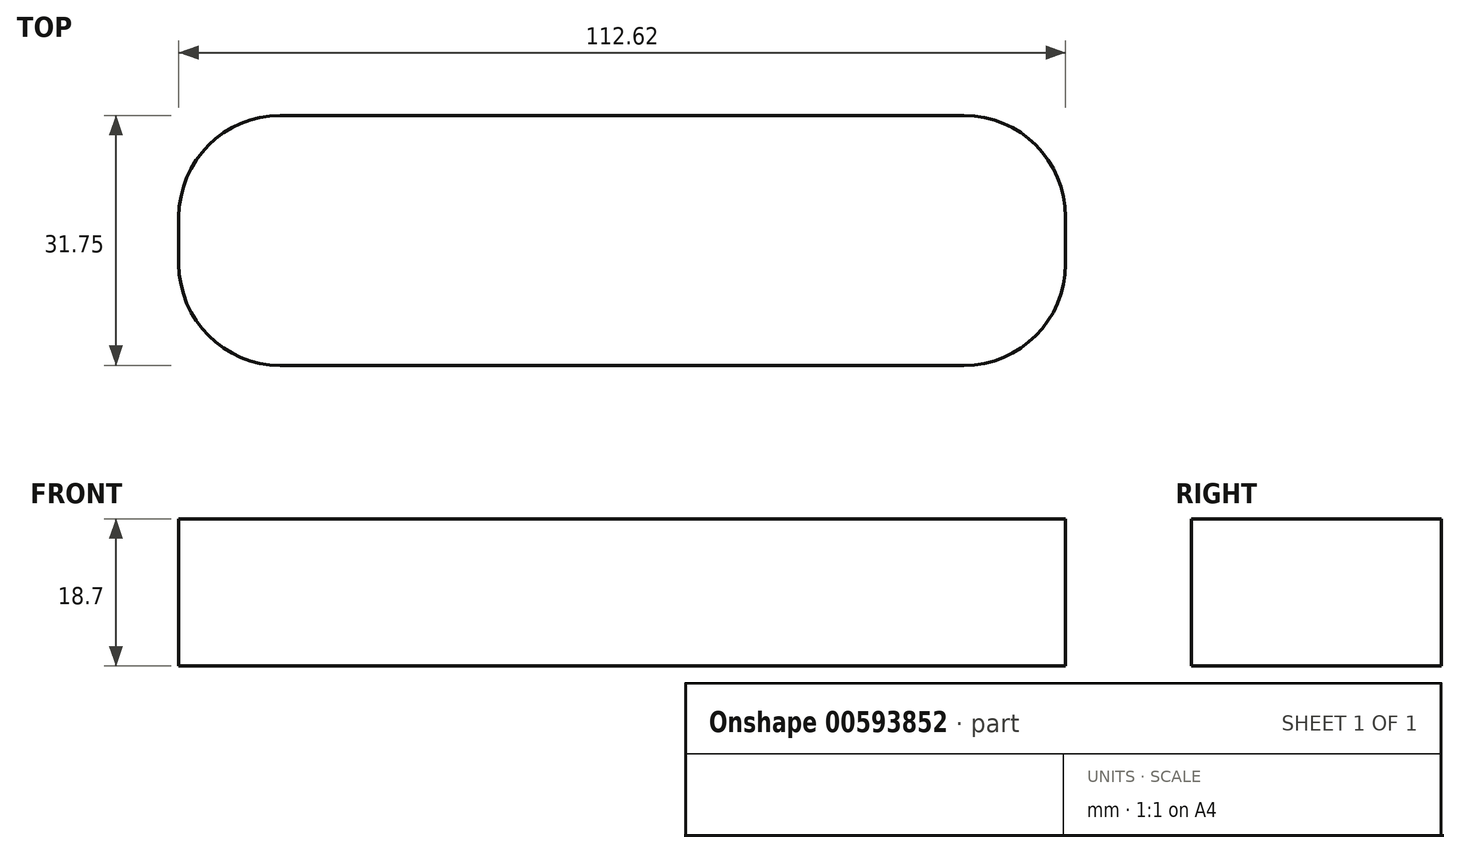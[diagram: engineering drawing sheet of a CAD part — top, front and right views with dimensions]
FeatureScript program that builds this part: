
annotation { "Feature Type Name" : "Feature", "Feature Type Description" : "" }
export const myFeature = defineFeature(function(context is Context, id is Id, definition is map)
    precondition{}
    {
        {
            var Q0;
            Q0=qCreatedBy(makeId("Front.planeOp"),FACE);
            var sketch = newSketch(context, id + "F0", { "sketchPlane" : qUnion([Q0])});
            skLineSegment(sketch, "E0.bottom", {"start": v(-56.31, 9.35) * mm, "end": v(56.31, 9.35) * mm});
            skLineSegment(sketch, "E0.top", {"start": v(-56.31, -9.35) * mm, "end": v(56.31, -9.35) * mm});
            skLineSegment(sketch, "E0.left", {"start": v(-56.31, 9.35) * mm, "end": v(-56.31, -9.35) * mm});
            skLineSegment(sketch, "E0.right", {"start": v(56.31, 9.35) * mm, "end": v(56.31, -9.35) * mm});
            skPoint(sketch, "E0.middle", {"position": v(0, 0) * mm});
            skSolve(sketch);
        }
        {
            var Q0;
            Q0 = qSketchRegion(id + "F0", true);
            extrude(context, id + "F1", {"entities" : qUnion([Q0]), "depth" : 31.75 * mm, "offsetDistance" : 25.4 * mm});
        }
        {
            var Q0;
            Q0=makeQuery(id+"F1.opExtrude","CAP_EDGE",EDGE,{"disambiguationData":[OSD([sQuery(id+"F0.wireOp",EDGE,"E0.right")])],"isStart":true});
            var Q1;
            Q1=makeQuery(id+"F1.opExtrude","CAP_EDGE",EDGE,{"disambiguationData":[OSD([sQuery(id+"F0.wireOp",EDGE,"E0.right")])],"isStart":false});
            fillet(context, id + "F2", {"entities" : qUnion([Q0, Q1]), "radius" : 12.88 * mm, "tangentPropagation" : true, "allowEdgeOverflow" : false});
        }
        {
            var Q0;
            Q0=makeQuery(id+"F1.opExtrude","CAP_EDGE",EDGE,{"disambiguationData":[OSD([sQuery(id+"F0.wireOp",EDGE,"E0.left")])],"isStart":true});
            var Q1;
            Q1=makeQuery(id+"F1.opExtrude","CAP_EDGE",EDGE,{"disambiguationData":[OSD([sQuery(id+"F0.wireOp",EDGE,"E0.left")])],"isStart":false});
            fillet(context, id + "F3", {"entities" : qUnion([Q0, Q1]), "radius" : 12.88 * mm, "tangentPropagation" : true, "allowEdgeOverflow" : false});
        }
    });
